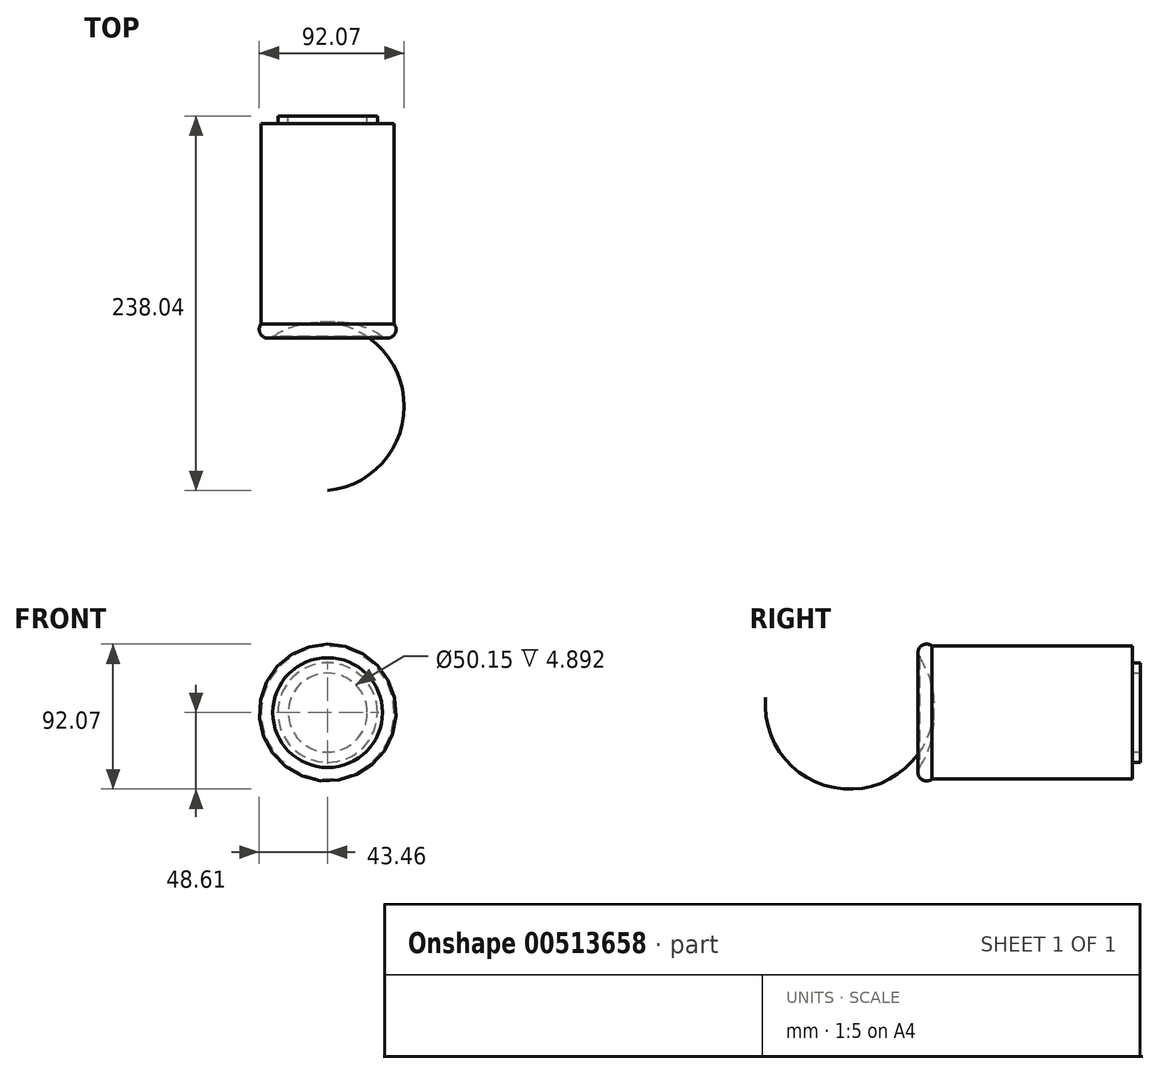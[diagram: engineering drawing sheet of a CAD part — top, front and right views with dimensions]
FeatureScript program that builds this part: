
annotation { "Feature Type Name" : "Feature", "Feature Type Description" : "" }
export const myFeature = defineFeature(function(context is Context, id is Id, definition is map)
    precondition{}
    {
        {
            var Q0;
            Q0=qCreatedBy(makeId("Top.planeOp"),FACE);
            var sketch = newSketch(context, id + "F0", { "sketchPlane" : qUnion([Q0])});
            skArc(sketch, "E0", {"start": v(34.86, -74.16) * mm, "mid": v(18.2, -66.65) * mm, "end": v(0, -65.19) * mm});
            skArc(sketch, "E1", {"start": v(34.86, -74.16) * mm, "mid": v(42.04, -73.24) * mm, "end": v(42.2, -66) * mm});
            skLineSegment(sketch, "E2", {"start": v(42.2, -66) * mm, "end": v(42.2, 61.2) * mm});
            skLineSegment(sketch, "E3", {"start": v(42.2, 61.2) * mm, "end": v(31.6, 61.2) * mm});
            skLineSegment(sketch, "E4", {"start": v(31.6, 61.2) * mm, "end": v(31.6, 66.1) * mm});
            skLineSegment(sketch, "E5", {"start": v(31.6, 66.1) * mm, "end": v(25.08, 66.1) * mm});
            skLineSegment(sketch, "E6", {"start": v(25.08, 66.1) * mm, "end": v(25.08, 61.2) * mm});
            skLineSegment(sketch, "E7", {"start": v(25.08, 61.2) * mm, "end": v(0, 61.2) * mm});
            skLineSegment(sketch, "E8", {"start": v(0, 61.2) * mm, "end": v(0, -65.19) * mm});
            skLineSegment(sketch, "E9", {"start": v(0, 73.43) * mm, "end": v(0, -80.68) * mm, "construction": true});
            skSolve(sketch);
        }
        {
            var Q0;
            Q0=makeQuery(id+"F0.imprint","IMPRINT",FACE,{"disambiguationData":[TD([[makeQuery(id+"F0.imprint","IMPRINT",EDGE,{"derivedFrom":sQuery(id+"F0.wireOp",EDGE,"E0")}),-1.0]])]});
            var Q1;
            Q1=sQuery(id+"F0.wireOp",EDGE,"E9");
            revolve(context, id + "F1", {"entities" : qUnion([Q0]), "axis" : qUnion([Q1]), "revolveType" : RevolveType.FULL});
        }
    });
